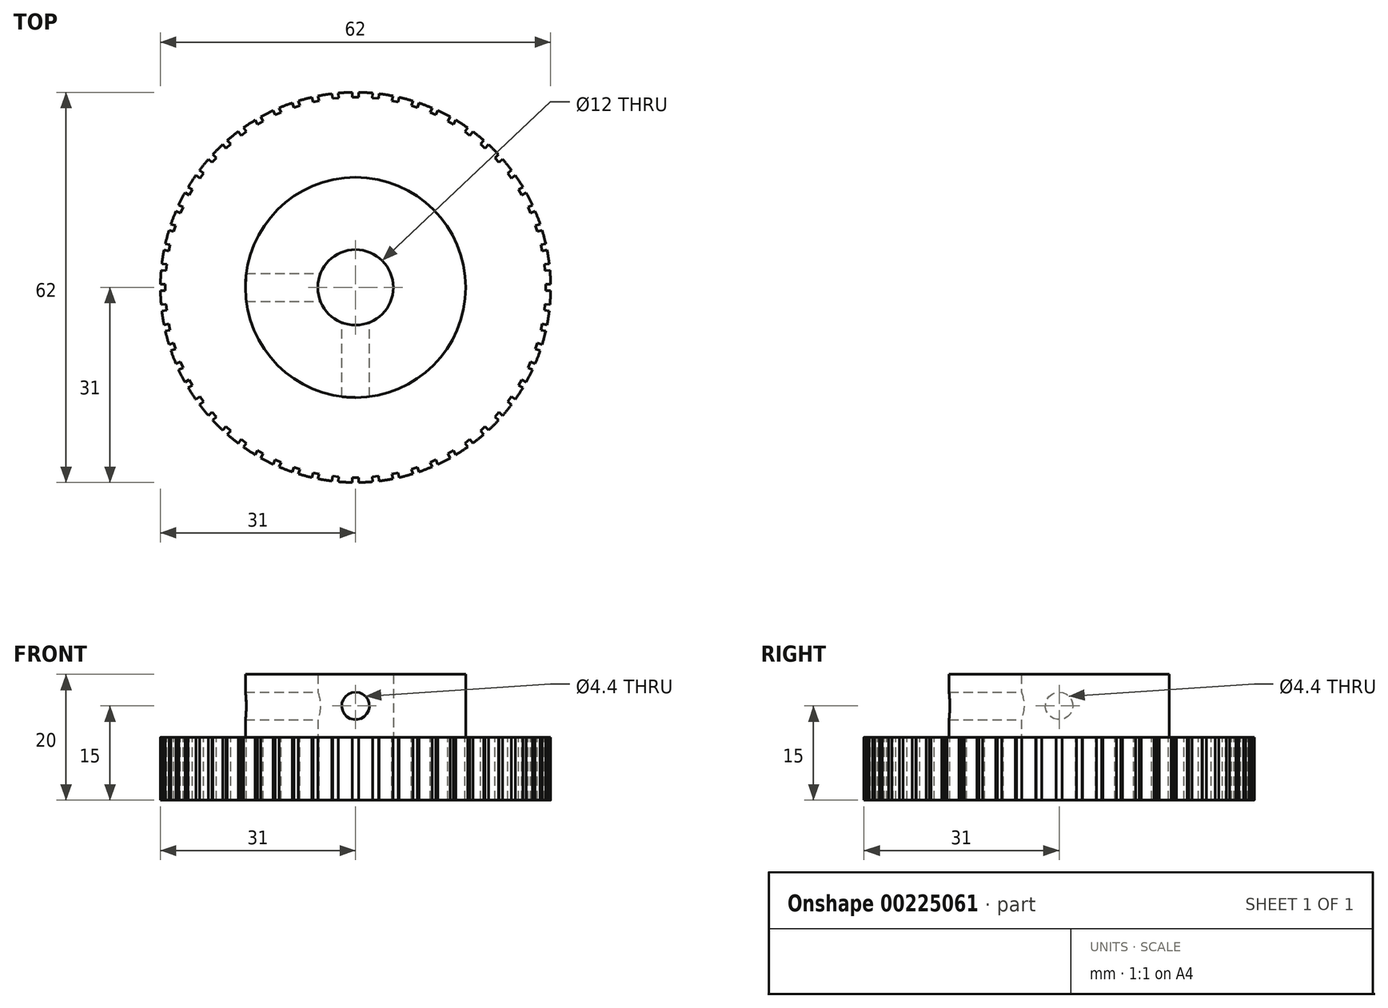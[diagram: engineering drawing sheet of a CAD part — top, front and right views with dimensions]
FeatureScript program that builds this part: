
annotation { "Feature Type Name" : "Feature", "Feature Type Description" : "" }
export const myFeature = defineFeature(function(context is Context, id is Id, definition is map)
    precondition{}
    {
        {
            var Q0;
            Q0=qCreatedBy(makeId("Top.planeOp"),FACE);
            var sketch = newSketch(context, id + "F0", { "sketchPlane" : qUnion([Q0])});
            skCircle(sketch, "E0", {"center": v(0, 0) * mm, "radius": 31 * mm});
            skCircle(sketch, "E1", {"center": v(0, 0) * mm, "radius": 6 * mm});
            skSolve(sketch);
        }
        {
            var Q0;
            Q0=qSketchRegion(id+"F0",true);
            extrude(context, id + "F1", {"entities" : qUnion([Q0]), "depth" : 10 * mm});
        }
        {
            var Q0;
            Q0=makeQuery(id+"F1.opExtrude","CAP_FACE",FACE,{"disambiguationData":[OSD([sQuery(id+"F0.wireOp",EDGE,"E0"),sQuery(id+"F0.wireOp",EDGE,"E1")])],"isStart":false});
            var sketch = newSketch(context, id + "F2", { "sketchPlane" : qUnion([Q0])});
            skCircle(sketch, "E2", {"center": v(0, 0) * mm, "radius": 17.5 * mm});
            skCircle(sketch, "E3", {"center": v(0, 0) * mm, "radius": 6 * mm});
            skSolve(sketch);
        }
        {
            var Q0;
            Q0=qSketchRegion(id+"F2",true);
            extrude(context, id + "F3", {"entities" : qUnion([Q0]), "operationType" : NewBodyOperationType.ADD, "depth" : 10 * mm});
        }
        {
            var Q0;
            Q0=makeQuery(id+"F1.opExtrude","CAP_FACE",FACE,{"disambiguationData":[OSD([sQuery(id+"F0.wireOp",EDGE,"E0"),sQuery(id+"F0.wireOp",EDGE,"E1")])],"isStart":false});
            var sketch = newSketch(context, id + "F4", { "sketchPlane" : qUnion([Q0])});
            skLineSegment(sketch, "E4.bottom", {"start": v(-0.5, 35.22) * mm, "end": v(0.5, 35.22) * mm});
            skLineSegment(sketch, "E4.top", {"start": v(-0.5, 30.22) * mm, "end": v(0.5, 30.22) * mm});
            skLineSegment(sketch, "E4.left", {"start": v(-0.5, 35.22) * mm, "end": v(-0.5, 30.22) * mm});
            skLineSegment(sketch, "E4.right", {"start": v(0.5, 35.22) * mm, "end": v(0.5, 30.22) * mm});
            skLineSegment(sketch, "E5.1.0", {"start": v(-3.18, 35.08) * mm, "end": v(-2.66, 30.1) * mm});
            skLineSegment(sketch, "E5.1.1", {"start": v(-4.18, 34.97) * mm, "end": v(-3.66, 30) * mm});
            skLineSegment(sketch, "E5.1.2", {"start": v(-3.66, 30) * mm, "end": v(-2.66, 30.1) * mm});
            skLineSegment(sketch, "E5.1.3", {"start": v(-4.18, 34.97) * mm, "end": v(-3.18, 35.08) * mm});
            skLineSegment(sketch, "E5.2.0", {"start": v(-6.83, 34.55) * mm, "end": v(-5.8, 29.66) * mm});
            skLineSegment(sketch, "E5.2.1", {"start": v(-7.81, 34.34) * mm, "end": v(-6.77, 29.45) * mm});
            skLineSegment(sketch, "E5.2.2", {"start": v(-6.77, 29.45) * mm, "end": v(-5.8, 29.66) * mm});
            skLineSegment(sketch, "E5.2.3", {"start": v(-7.81, 34.34) * mm, "end": v(-6.83, 34.55) * mm});
            skLineSegment(sketch, "E5.3.0", {"start": v(-10.4, 33.65) * mm, "end": v(-8.86, 28.9) * mm});
            skLineSegment(sketch, "E5.3.1", {"start": v(-11.36, 33.34) * mm, "end": v(-9.81, 28.58) * mm});
            skLineSegment(sketch, "E5.3.2", {"start": v(-9.81, 28.58) * mm, "end": v(-8.86, 28.9) * mm});
            skLineSegment(sketch, "E5.3.3", {"start": v(-11.36, 33.34) * mm, "end": v(-10.4, 33.65) * mm});
            skLineSegment(sketch, "E5.4.0", {"start": v(-13.87, 32.38) * mm, "end": v(-11.83, 27.8) * mm});
            skLineSegment(sketch, "E5.4.1", {"start": v(-14.78, 31.97) * mm, "end": v(-12.75, 27.4) * mm});
            skLineSegment(sketch, "E5.4.2", {"start": v(-12.75, 27.4) * mm, "end": v(-11.83, 27.8) * mm});
            skLineSegment(sketch, "E5.4.3", {"start": v(-14.78, 31.97) * mm, "end": v(-13.87, 32.38) * mm});
            skLineSegment(sketch, "E5.5.0", {"start": v(-17.18, 30.75) * mm, "end": v(-14.68, 26.42) * mm});
            skLineSegment(sketch, "E5.5.1", {"start": v(-18.04, 30.25) * mm, "end": v(-15.54, 25.92) * mm});
            skLineSegment(sketch, "E5.5.2", {"start": v(-15.54, 25.92) * mm, "end": v(-14.68, 26.42) * mm});
            skLineSegment(sketch, "E5.5.3", {"start": v(-18.04, 30.25) * mm, "end": v(-17.18, 30.75) * mm});
            skLineSegment(sketch, "E5.6.0", {"start": v(-20.3, 28.78) * mm, "end": v(-17.36, 24.74) * mm});
            skLineSegment(sketch, "E5.6.1", {"start": v(-21.1, 28.2) * mm, "end": v(-18.17, 24.15) * mm});
            skLineSegment(sketch, "E5.6.2", {"start": v(-18.17, 24.15) * mm, "end": v(-17.36, 24.74) * mm});
            skLineSegment(sketch, "E5.6.3", {"start": v(-21.1, 28.2) * mm, "end": v(-20.3, 28.78) * mm});
            skLineSegment(sketch, "E5.7.0", {"start": v(-23.2, 26.5) * mm, "end": v(-19.85, 22.8) * mm});
            skLineSegment(sketch, "E5.7.1", {"start": v(-23.94, 25.84) * mm, "end": v(-20.6, 22.12) * mm});
            skLineSegment(sketch, "E5.7.2", {"start": v(-20.6, 22.12) * mm, "end": v(-19.85, 22.8) * mm});
            skLineSegment(sketch, "E5.7.3", {"start": v(-23.94, 25.84) * mm, "end": v(-23.2, 26.5) * mm});
            skLineSegment(sketch, "E5.8.0", {"start": v(-25.84, 23.94) * mm, "end": v(-22.12, 20.6) * mm});
            skLineSegment(sketch, "E5.8.1", {"start": v(-26.5, 23.2) * mm, "end": v(-22.8, 19.85) * mm});
            skLineSegment(sketch, "E5.8.2", {"start": v(-22.8, 19.85) * mm, "end": v(-22.12, 20.6) * mm});
            skLineSegment(sketch, "E5.8.3", {"start": v(-26.5, 23.2) * mm, "end": v(-25.84, 23.94) * mm});
            skLineSegment(sketch, "E5.9.0", {"start": v(-28.2, 21.1) * mm, "end": v(-24.15, 18.17) * mm});
            skLineSegment(sketch, "E5.9.1", {"start": v(-28.78, 20.3) * mm, "end": v(-24.74, 17.36) * mm});
            skLineSegment(sketch, "E5.9.2", {"start": v(-24.74, 17.36) * mm, "end": v(-24.15, 18.17) * mm});
            skLineSegment(sketch, "E5.9.3", {"start": v(-28.78, 20.3) * mm, "end": v(-28.2, 21.1) * mm});
            skLineSegment(sketch, "E5.10.0", {"start": v(-30.25, 18.04) * mm, "end": v(-25.92, 15.54) * mm});
            skLineSegment(sketch, "E5.10.1", {"start": v(-30.75, 17.18) * mm, "end": v(-26.42, 14.68) * mm});
            skLineSegment(sketch, "E5.10.2", {"start": v(-26.42, 14.68) * mm, "end": v(-25.92, 15.54) * mm});
            skLineSegment(sketch, "E5.10.3", {"start": v(-30.75, 17.18) * mm, "end": v(-30.25, 18.04) * mm});
            skLineSegment(sketch, "E5.11.0", {"start": v(-31.97, 14.78) * mm, "end": v(-27.4, 12.75) * mm});
            skLineSegment(sketch, "E5.11.1", {"start": v(-32.38, 13.87) * mm, "end": v(-27.8, 11.83) * mm});
            skLineSegment(sketch, "E5.11.2", {"start": v(-27.8, 11.83) * mm, "end": v(-27.4, 12.75) * mm});
            skLineSegment(sketch, "E5.11.3", {"start": v(-32.38, 13.87) * mm, "end": v(-31.97, 14.78) * mm});
            skLineSegment(sketch, "E5.12.0", {"start": v(-33.34, 11.36) * mm, "end": v(-28.58, 9.81) * mm});
            skLineSegment(sketch, "E5.12.1", {"start": v(-33.65, 10.4) * mm, "end": v(-28.9, 8.86) * mm});
            skLineSegment(sketch, "E5.12.2", {"start": v(-28.9, 8.86) * mm, "end": v(-28.58, 9.81) * mm});
            skLineSegment(sketch, "E5.12.3", {"start": v(-33.65, 10.4) * mm, "end": v(-33.34, 11.36) * mm});
            skLineSegment(sketch, "E5.13.0", {"start": v(-34.34, 7.81) * mm, "end": v(-29.45, 6.77) * mm});
            skLineSegment(sketch, "E5.13.1", {"start": v(-34.55, 6.83) * mm, "end": v(-29.66, 5.8) * mm});
            skLineSegment(sketch, "E5.13.2", {"start": v(-29.66, 5.8) * mm, "end": v(-29.45, 6.77) * mm});
            skLineSegment(sketch, "E5.13.3", {"start": v(-34.55, 6.83) * mm, "end": v(-34.34, 7.81) * mm});
            skLineSegment(sketch, "E5.14.0", {"start": v(-34.97, 4.18) * mm, "end": v(-30, 3.66) * mm});
            skLineSegment(sketch, "E5.14.1", {"start": v(-35.08, 3.18) * mm, "end": v(-30.1, 2.66) * mm});
            skLineSegment(sketch, "E5.14.2", {"start": v(-30.1, 2.66) * mm, "end": v(-30, 3.66) * mm});
            skLineSegment(sketch, "E5.14.3", {"start": v(-35.08, 3.18) * mm, "end": v(-34.97, 4.18) * mm});
            skLineSegment(sketch, "E5.15.0", {"start": v(-35.22, 0.5) * mm, "end": v(-30.22, 0.5) * mm});
            skLineSegment(sketch, "E5.15.1", {"start": v(-35.22, -0.5) * mm, "end": v(-30.22, -0.5) * mm});
            skLineSegment(sketch, "E5.15.2", {"start": v(-30.22, -0.5) * mm, "end": v(-30.22, 0.5) * mm});
            skLineSegment(sketch, "E5.15.3", {"start": v(-35.22, -0.5) * mm, "end": v(-35.22, 0.5) * mm});
            skLineSegment(sketch, "E5.16.0", {"start": v(-35.08, -3.18) * mm, "end": v(-30.1, -2.66) * mm});
            skLineSegment(sketch, "E5.16.1", {"start": v(-34.97, -4.18) * mm, "end": v(-30, -3.66) * mm});
            skLineSegment(sketch, "E5.16.2", {"start": v(-30, -3.66) * mm, "end": v(-30.1, -2.66) * mm});
            skLineSegment(sketch, "E5.16.3", {"start": v(-34.97, -4.18) * mm, "end": v(-35.08, -3.18) * mm});
            skLineSegment(sketch, "E5.17.0", {"start": v(-34.55, -6.83) * mm, "end": v(-29.66, -5.8) * mm});
            skLineSegment(sketch, "E5.17.1", {"start": v(-34.34, -7.81) * mm, "end": v(-29.45, -6.77) * mm});
            skLineSegment(sketch, "E5.17.2", {"start": v(-29.45, -6.77) * mm, "end": v(-29.66, -5.8) * mm});
            skLineSegment(sketch, "E5.17.3", {"start": v(-34.34, -7.81) * mm, "end": v(-34.55, -6.83) * mm});
            skLineSegment(sketch, "E5.18.0", {"start": v(-33.65, -10.4) * mm, "end": v(-28.9, -8.86) * mm});
            skLineSegment(sketch, "E5.18.1", {"start": v(-33.34, -11.36) * mm, "end": v(-28.58, -9.81) * mm});
            skLineSegment(sketch, "E5.18.2", {"start": v(-28.58, -9.81) * mm, "end": v(-28.9, -8.86) * mm});
            skLineSegment(sketch, "E5.18.3", {"start": v(-33.34, -11.36) * mm, "end": v(-33.65, -10.4) * mm});
            skLineSegment(sketch, "E5.19.0", {"start": v(-32.38, -13.87) * mm, "end": v(-27.8, -11.83) * mm});
            skLineSegment(sketch, "E5.19.1", {"start": v(-31.97, -14.78) * mm, "end": v(-27.4, -12.75) * mm});
            skLineSegment(sketch, "E5.19.2", {"start": v(-27.4, -12.75) * mm, "end": v(-27.8, -11.83) * mm});
            skLineSegment(sketch, "E5.19.3", {"start": v(-31.97, -14.78) * mm, "end": v(-32.38, -13.87) * mm});
            skLineSegment(sketch, "E5.20.0", {"start": v(-30.75, -17.18) * mm, "end": v(-26.42, -14.68) * mm});
            skLineSegment(sketch, "E5.20.1", {"start": v(-30.25, -18.04) * mm, "end": v(-25.92, -15.54) * mm});
            skLineSegment(sketch, "E5.20.2", {"start": v(-25.92, -15.54) * mm, "end": v(-26.42, -14.68) * mm});
            skLineSegment(sketch, "E5.20.3", {"start": v(-30.25, -18.04) * mm, "end": v(-30.75, -17.18) * mm});
            skLineSegment(sketch, "E5.21.0", {"start": v(-28.78, -20.3) * mm, "end": v(-24.74, -17.36) * mm});
            skLineSegment(sketch, "E5.21.1", {"start": v(-28.2, -21.1) * mm, "end": v(-24.15, -18.17) * mm});
            skLineSegment(sketch, "E5.21.2", {"start": v(-24.15, -18.17) * mm, "end": v(-24.74, -17.36) * mm});
            skLineSegment(sketch, "E5.21.3", {"start": v(-28.2, -21.1) * mm, "end": v(-28.78, -20.3) * mm});
            skLineSegment(sketch, "E5.22.0", {"start": v(-26.5, -23.2) * mm, "end": v(-22.8, -19.85) * mm});
            skLineSegment(sketch, "E5.22.1", {"start": v(-25.84, -23.94) * mm, "end": v(-22.12, -20.6) * mm});
            skLineSegment(sketch, "E5.22.2", {"start": v(-22.12, -20.6) * mm, "end": v(-22.8, -19.85) * mm});
            skLineSegment(sketch, "E5.22.3", {"start": v(-25.84, -23.94) * mm, "end": v(-26.5, -23.2) * mm});
            skLineSegment(sketch, "E5.23.0", {"start": v(-23.94, -25.84) * mm, "end": v(-20.6, -22.12) * mm});
            skLineSegment(sketch, "E5.23.1", {"start": v(-23.2, -26.5) * mm, "end": v(-19.85, -22.8) * mm});
            skLineSegment(sketch, "E5.23.2", {"start": v(-19.85, -22.8) * mm, "end": v(-20.6, -22.12) * mm});
            skLineSegment(sketch, "E5.23.3", {"start": v(-23.2, -26.5) * mm, "end": v(-23.94, -25.84) * mm});
            skLineSegment(sketch, "E5.24.0", {"start": v(-21.1, -28.2) * mm, "end": v(-18.17, -24.15) * mm});
            skLineSegment(sketch, "E5.24.1", {"start": v(-20.3, -28.78) * mm, "end": v(-17.36, -24.74) * mm});
            skLineSegment(sketch, "E5.24.2", {"start": v(-17.36, -24.74) * mm, "end": v(-18.17, -24.15) * mm});
            skLineSegment(sketch, "E5.24.3", {"start": v(-20.3, -28.78) * mm, "end": v(-21.1, -28.2) * mm});
            skLineSegment(sketch, "E5.25.0", {"start": v(-18.04, -30.25) * mm, "end": v(-15.54, -25.92) * mm});
            skLineSegment(sketch, "E5.25.1", {"start": v(-17.18, -30.75) * mm, "end": v(-14.68, -26.42) * mm});
            skLineSegment(sketch, "E5.25.2", {"start": v(-14.68, -26.42) * mm, "end": v(-15.54, -25.92) * mm});
            skLineSegment(sketch, "E5.25.3", {"start": v(-17.18, -30.75) * mm, "end": v(-18.04, -30.25) * mm});
            skLineSegment(sketch, "E5.26.0", {"start": v(-14.78, -31.97) * mm, "end": v(-12.75, -27.4) * mm});
            skLineSegment(sketch, "E5.26.1", {"start": v(-13.87, -32.38) * mm, "end": v(-11.83, -27.8) * mm});
            skLineSegment(sketch, "E5.26.2", {"start": v(-11.83, -27.8) * mm, "end": v(-12.75, -27.4) * mm});
            skLineSegment(sketch, "E5.26.3", {"start": v(-13.87, -32.38) * mm, "end": v(-14.78, -31.97) * mm});
            skLineSegment(sketch, "E5.27.0", {"start": v(-11.36, -33.34) * mm, "end": v(-9.81, -28.58) * mm});
            skLineSegment(sketch, "E5.27.1", {"start": v(-10.4, -33.65) * mm, "end": v(-8.86, -28.9) * mm});
            skLineSegment(sketch, "E5.27.2", {"start": v(-8.86, -28.9) * mm, "end": v(-9.81, -28.58) * mm});
            skLineSegment(sketch, "E5.27.3", {"start": v(-10.4, -33.65) * mm, "end": v(-11.36, -33.34) * mm});
            skLineSegment(sketch, "E5.28.0", {"start": v(-7.81, -34.34) * mm, "end": v(-6.77, -29.45) * mm});
            skLineSegment(sketch, "E5.28.1", {"start": v(-6.83, -34.55) * mm, "end": v(-5.8, -29.66) * mm});
            skLineSegment(sketch, "E5.28.2", {"start": v(-5.8, -29.66) * mm, "end": v(-6.77, -29.45) * mm});
            skLineSegment(sketch, "E5.28.3", {"start": v(-6.83, -34.55) * mm, "end": v(-7.81, -34.34) * mm});
            skLineSegment(sketch, "E5.29.0", {"start": v(-4.18, -34.97) * mm, "end": v(-3.66, -30) * mm});
            skLineSegment(sketch, "E5.29.1", {"start": v(-3.18, -35.08) * mm, "end": v(-2.66, -30.1) * mm});
            skLineSegment(sketch, "E5.29.2", {"start": v(-2.66, -30.1) * mm, "end": v(-3.66, -30) * mm});
            skLineSegment(sketch, "E5.29.3", {"start": v(-3.18, -35.08) * mm, "end": v(-4.18, -34.97) * mm});
            skLineSegment(sketch, "E5.30.0", {"start": v(-0.5, -35.22) * mm, "end": v(-0.5, -30.22) * mm});
            skLineSegment(sketch, "E5.30.1", {"start": v(0.5, -35.22) * mm, "end": v(0.5, -30.22) * mm});
            skLineSegment(sketch, "E5.30.2", {"start": v(0.5, -30.22) * mm, "end": v(-0.5, -30.22) * mm});
            skLineSegment(sketch, "E5.30.3", {"start": v(0.5, -35.22) * mm, "end": v(-0.5, -35.22) * mm});
            skLineSegment(sketch, "E5.31.0", {"start": v(3.18, -35.08) * mm, "end": v(2.66, -30.1) * mm});
            skLineSegment(sketch, "E5.31.1", {"start": v(4.18, -34.97) * mm, "end": v(3.66, -30) * mm});
            skLineSegment(sketch, "E5.31.2", {"start": v(3.66, -30) * mm, "end": v(2.66, -30.1) * mm});
            skLineSegment(sketch, "E5.31.3", {"start": v(4.18, -34.97) * mm, "end": v(3.18, -35.08) * mm});
            skLineSegment(sketch, "E5.32.0", {"start": v(6.83, -34.55) * mm, "end": v(5.8, -29.66) * mm});
            skLineSegment(sketch, "E5.32.1", {"start": v(7.81, -34.34) * mm, "end": v(6.77, -29.45) * mm});
            skLineSegment(sketch, "E5.32.2", {"start": v(6.77, -29.45) * mm, "end": v(5.8, -29.66) * mm});
            skLineSegment(sketch, "E5.32.3", {"start": v(7.81, -34.34) * mm, "end": v(6.83, -34.55) * mm});
            skLineSegment(sketch, "E5.33.0", {"start": v(10.4, -33.65) * mm, "end": v(8.86, -28.9) * mm});
            skLineSegment(sketch, "E5.33.1", {"start": v(11.36, -33.34) * mm, "end": v(9.81, -28.58) * mm});
            skLineSegment(sketch, "E5.33.2", {"start": v(9.81, -28.58) * mm, "end": v(8.86, -28.9) * mm});
            skLineSegment(sketch, "E5.33.3", {"start": v(11.36, -33.34) * mm, "end": v(10.4, -33.65) * mm});
            skLineSegment(sketch, "E5.34.0", {"start": v(13.87, -32.38) * mm, "end": v(11.83, -27.8) * mm});
            skLineSegment(sketch, "E5.34.1", {"start": v(14.78, -31.97) * mm, "end": v(12.75, -27.4) * mm});
            skLineSegment(sketch, "E5.34.2", {"start": v(12.75, -27.4) * mm, "end": v(11.83, -27.8) * mm});
            skLineSegment(sketch, "E5.34.3", {"start": v(14.78, -31.97) * mm, "end": v(13.87, -32.38) * mm});
            skLineSegment(sketch, "E5.35.0", {"start": v(17.18, -30.75) * mm, "end": v(14.68, -26.42) * mm});
            skLineSegment(sketch, "E5.35.1", {"start": v(18.04, -30.25) * mm, "end": v(15.54, -25.92) * mm});
            skLineSegment(sketch, "E5.35.2", {"start": v(15.54, -25.92) * mm, "end": v(14.68, -26.42) * mm});
            skLineSegment(sketch, "E5.35.3", {"start": v(18.04, -30.25) * mm, "end": v(17.18, -30.75) * mm});
            skLineSegment(sketch, "E5.36.0", {"start": v(20.3, -28.78) * mm, "end": v(17.36, -24.74) * mm});
            skLineSegment(sketch, "E5.36.1", {"start": v(21.1, -28.2) * mm, "end": v(18.17, -24.15) * mm});
            skLineSegment(sketch, "E5.36.2", {"start": v(18.17, -24.15) * mm, "end": v(17.36, -24.74) * mm});
            skLineSegment(sketch, "E5.36.3", {"start": v(21.1, -28.2) * mm, "end": v(20.3, -28.78) * mm});
            skLineSegment(sketch, "E5.37.0", {"start": v(23.2, -26.5) * mm, "end": v(19.85, -22.8) * mm});
            skLineSegment(sketch, "E5.37.1", {"start": v(23.94, -25.84) * mm, "end": v(20.6, -22.12) * mm});
            skLineSegment(sketch, "E5.37.2", {"start": v(20.6, -22.12) * mm, "end": v(19.85, -22.8) * mm});
            skLineSegment(sketch, "E5.37.3", {"start": v(23.94, -25.84) * mm, "end": v(23.2, -26.5) * mm});
            skLineSegment(sketch, "E5.38.0", {"start": v(25.84, -23.94) * mm, "end": v(22.12, -20.6) * mm});
            skLineSegment(sketch, "E5.38.1", {"start": v(26.5, -23.2) * mm, "end": v(22.8, -19.85) * mm});
            skLineSegment(sketch, "E5.38.2", {"start": v(22.8, -19.85) * mm, "end": v(22.12, -20.6) * mm});
            skLineSegment(sketch, "E5.38.3", {"start": v(26.5, -23.2) * mm, "end": v(25.84, -23.94) * mm});
            skLineSegment(sketch, "E5.39.0", {"start": v(28.2, -21.1) * mm, "end": v(24.15, -18.17) * mm});
            skLineSegment(sketch, "E5.39.1", {"start": v(28.78, -20.3) * mm, "end": v(24.74, -17.36) * mm});
            skLineSegment(sketch, "E5.39.2", {"start": v(24.74, -17.36) * mm, "end": v(24.15, -18.17) * mm});
            skLineSegment(sketch, "E5.39.3", {"start": v(28.78, -20.3) * mm, "end": v(28.2, -21.1) * mm});
            skLineSegment(sketch, "E5.40.0", {"start": v(30.25, -18.04) * mm, "end": v(25.92, -15.54) * mm});
            skLineSegment(sketch, "E5.40.1", {"start": v(30.75, -17.18) * mm, "end": v(26.42, -14.68) * mm});
            skLineSegment(sketch, "E5.40.2", {"start": v(26.42, -14.68) * mm, "end": v(25.92, -15.54) * mm});
            skLineSegment(sketch, "E5.40.3", {"start": v(30.75, -17.18) * mm, "end": v(30.25, -18.04) * mm});
            skLineSegment(sketch, "E5.41.0", {"start": v(31.97, -14.78) * mm, "end": v(27.4, -12.75) * mm});
            skLineSegment(sketch, "E5.41.1", {"start": v(32.38, -13.87) * mm, "end": v(27.8, -11.83) * mm});
            skLineSegment(sketch, "E5.41.2", {"start": v(27.8, -11.83) * mm, "end": v(27.4, -12.75) * mm});
            skLineSegment(sketch, "E5.41.3", {"start": v(32.38, -13.87) * mm, "end": v(31.97, -14.78) * mm});
            skLineSegment(sketch, "E5.42.0", {"start": v(33.34, -11.36) * mm, "end": v(28.58, -9.81) * mm});
            skLineSegment(sketch, "E5.42.1", {"start": v(33.65, -10.4) * mm, "end": v(28.9, -8.86) * mm});
            skLineSegment(sketch, "E5.42.2", {"start": v(28.9, -8.86) * mm, "end": v(28.58, -9.81) * mm});
            skLineSegment(sketch, "E5.42.3", {"start": v(33.65, -10.4) * mm, "end": v(33.34, -11.36) * mm});
            skLineSegment(sketch, "E5.43.0", {"start": v(34.34, -7.81) * mm, "end": v(29.45, -6.77) * mm});
            skLineSegment(sketch, "E5.43.1", {"start": v(34.55, -6.83) * mm, "end": v(29.66, -5.8) * mm});
            skLineSegment(sketch, "E5.43.2", {"start": v(29.66, -5.8) * mm, "end": v(29.45, -6.77) * mm});
            skLineSegment(sketch, "E5.43.3", {"start": v(34.55, -6.83) * mm, "end": v(34.34, -7.81) * mm});
            skLineSegment(sketch, "E5.44.0", {"start": v(34.97, -4.18) * mm, "end": v(30, -3.66) * mm});
            skLineSegment(sketch, "E5.44.1", {"start": v(35.08, -3.18) * mm, "end": v(30.1, -2.66) * mm});
            skLineSegment(sketch, "E5.44.2", {"start": v(30.1, -2.66) * mm, "end": v(30, -3.66) * mm});
            skLineSegment(sketch, "E5.44.3", {"start": v(35.08, -3.18) * mm, "end": v(34.97, -4.18) * mm});
            skLineSegment(sketch, "E5.45.0", {"start": v(35.22, -0.5) * mm, "end": v(30.22, -0.5) * mm});
            skLineSegment(sketch, "E5.45.1", {"start": v(35.22, 0.5) * mm, "end": v(30.22, 0.5) * mm});
            skLineSegment(sketch, "E5.45.2", {"start": v(30.22, 0.5) * mm, "end": v(30.22, -0.5) * mm});
            skLineSegment(sketch, "E5.45.3", {"start": v(35.22, 0.5) * mm, "end": v(35.22, -0.5) * mm});
            skLineSegment(sketch, "E5.46.0", {"start": v(35.08, 3.18) * mm, "end": v(30.1, 2.66) * mm});
            skLineSegment(sketch, "E5.46.1", {"start": v(34.97, 4.18) * mm, "end": v(30, 3.66) * mm});
            skLineSegment(sketch, "E5.46.2", {"start": v(30, 3.66) * mm, "end": v(30.1, 2.66) * mm});
            skLineSegment(sketch, "E5.46.3", {"start": v(34.97, 4.18) * mm, "end": v(35.08, 3.18) * mm});
            skLineSegment(sketch, "E5.47.0", {"start": v(34.55, 6.83) * mm, "end": v(29.66, 5.8) * mm});
            skLineSegment(sketch, "E5.47.1", {"start": v(34.34, 7.81) * mm, "end": v(29.45, 6.77) * mm});
            skLineSegment(sketch, "E5.47.2", {"start": v(29.45, 6.77) * mm, "end": v(29.66, 5.8) * mm});
            skLineSegment(sketch, "E5.47.3", {"start": v(34.34, 7.81) * mm, "end": v(34.55, 6.83) * mm});
            skLineSegment(sketch, "E5.48.0", {"start": v(33.65, 10.4) * mm, "end": v(28.9, 8.86) * mm});
            skLineSegment(sketch, "E5.48.1", {"start": v(33.34, 11.36) * mm, "end": v(28.58, 9.81) * mm});
            skLineSegment(sketch, "E5.48.2", {"start": v(28.58, 9.81) * mm, "end": v(28.9, 8.86) * mm});
            skLineSegment(sketch, "E5.48.3", {"start": v(33.34, 11.36) * mm, "end": v(33.65, 10.4) * mm});
            skLineSegment(sketch, "E5.49.0", {"start": v(32.38, 13.87) * mm, "end": v(27.8, 11.83) * mm});
            skLineSegment(sketch, "E5.49.1", {"start": v(31.97, 14.78) * mm, "end": v(27.4, 12.75) * mm});
            skLineSegment(sketch, "E5.49.2", {"start": v(27.4, 12.75) * mm, "end": v(27.8, 11.83) * mm});
            skLineSegment(sketch, "E5.49.3", {"start": v(31.97, 14.78) * mm, "end": v(32.38, 13.87) * mm});
            skLineSegment(sketch, "E5.50.0", {"start": v(30.75, 17.18) * mm, "end": v(26.42, 14.68) * mm});
            skLineSegment(sketch, "E5.50.1", {"start": v(30.25, 18.04) * mm, "end": v(25.92, 15.54) * mm});
            skLineSegment(sketch, "E5.50.2", {"start": v(25.92, 15.54) * mm, "end": v(26.42, 14.68) * mm});
            skLineSegment(sketch, "E5.50.3", {"start": v(30.25, 18.04) * mm, "end": v(30.75, 17.18) * mm});
            skLineSegment(sketch, "E5.51.0", {"start": v(28.78, 20.3) * mm, "end": v(24.74, 17.36) * mm});
            skLineSegment(sketch, "E5.51.1", {"start": v(28.2, 21.1) * mm, "end": v(24.15, 18.17) * mm});
            skLineSegment(sketch, "E5.51.2", {"start": v(24.15, 18.17) * mm, "end": v(24.74, 17.36) * mm});
            skLineSegment(sketch, "E5.51.3", {"start": v(28.2, 21.1) * mm, "end": v(28.78, 20.3) * mm});
            skLineSegment(sketch, "E5.52.0", {"start": v(26.5, 23.2) * mm, "end": v(22.8, 19.85) * mm});
            skLineSegment(sketch, "E5.52.1", {"start": v(25.84, 23.94) * mm, "end": v(22.12, 20.6) * mm});
            skLineSegment(sketch, "E5.52.2", {"start": v(22.12, 20.6) * mm, "end": v(22.8, 19.85) * mm});
            skLineSegment(sketch, "E5.52.3", {"start": v(25.84, 23.94) * mm, "end": v(26.5, 23.2) * mm});
            skLineSegment(sketch, "E5.53.0", {"start": v(23.94, 25.84) * mm, "end": v(20.6, 22.12) * mm});
            skLineSegment(sketch, "E5.53.1", {"start": v(23.2, 26.5) * mm, "end": v(19.85, 22.8) * mm});
            skLineSegment(sketch, "E5.53.2", {"start": v(19.85, 22.8) * mm, "end": v(20.6, 22.12) * mm});
            skLineSegment(sketch, "E5.53.3", {"start": v(23.2, 26.5) * mm, "end": v(23.94, 25.84) * mm});
            skLineSegment(sketch, "E5.54.0", {"start": v(21.1, 28.2) * mm, "end": v(18.17, 24.15) * mm});
            skLineSegment(sketch, "E5.54.1", {"start": v(20.3, 28.78) * mm, "end": v(17.36, 24.74) * mm});
            skLineSegment(sketch, "E5.54.2", {"start": v(17.36, 24.74) * mm, "end": v(18.17, 24.15) * mm});
            skLineSegment(sketch, "E5.54.3", {"start": v(20.3, 28.78) * mm, "end": v(21.1, 28.2) * mm});
            skLineSegment(sketch, "E5.55.0", {"start": v(18.04, 30.25) * mm, "end": v(15.54, 25.92) * mm});
            skLineSegment(sketch, "E5.55.1", {"start": v(17.18, 30.75) * mm, "end": v(14.68, 26.42) * mm});
            skLineSegment(sketch, "E5.55.2", {"start": v(14.68, 26.42) * mm, "end": v(15.54, 25.92) * mm});
            skLineSegment(sketch, "E5.55.3", {"start": v(17.18, 30.75) * mm, "end": v(18.04, 30.25) * mm});
            skLineSegment(sketch, "E5.56.0", {"start": v(14.78, 31.97) * mm, "end": v(12.75, 27.4) * mm});
            skLineSegment(sketch, "E5.56.1", {"start": v(13.87, 32.38) * mm, "end": v(11.83, 27.8) * mm});
            skLineSegment(sketch, "E5.56.2", {"start": v(11.83, 27.8) * mm, "end": v(12.75, 27.4) * mm});
            skLineSegment(sketch, "E5.56.3", {"start": v(13.87, 32.38) * mm, "end": v(14.78, 31.97) * mm});
            skLineSegment(sketch, "E5.57.0", {"start": v(11.36, 33.34) * mm, "end": v(9.81, 28.58) * mm});
            skLineSegment(sketch, "E5.57.1", {"start": v(10.4, 33.65) * mm, "end": v(8.86, 28.9) * mm});
            skLineSegment(sketch, "E5.57.2", {"start": v(8.86, 28.9) * mm, "end": v(9.81, 28.58) * mm});
            skLineSegment(sketch, "E5.57.3", {"start": v(10.4, 33.65) * mm, "end": v(11.36, 33.34) * mm});
            skLineSegment(sketch, "E5.58.0", {"start": v(7.81, 34.34) * mm, "end": v(6.77, 29.45) * mm});
            skLineSegment(sketch, "E5.58.1", {"start": v(6.83, 34.55) * mm, "end": v(5.8, 29.66) * mm});
            skLineSegment(sketch, "E5.58.2", {"start": v(5.8, 29.66) * mm, "end": v(6.77, 29.45) * mm});
            skLineSegment(sketch, "E5.58.3", {"start": v(6.83, 34.55) * mm, "end": v(7.81, 34.34) * mm});
            skLineSegment(sketch, "E5.59.0", {"start": v(4.18, 34.97) * mm, "end": v(3.66, 30) * mm});
            skLineSegment(sketch, "E5.59.1", {"start": v(3.18, 35.08) * mm, "end": v(2.66, 30.1) * mm});
            skLineSegment(sketch, "E5.59.2", {"start": v(2.66, 30.1) * mm, "end": v(3.66, 30) * mm});
            skLineSegment(sketch, "E5.59.3", {"start": v(3.18, 35.08) * mm, "end": v(4.18, 34.97) * mm});
            skPoint(sketch, "E5.center", {"position": v(0, 0) * mm});
            skSolve(sketch);
        }
        {
            var Q0;
            Q0=qSketchRegion(id+"F4",true);
            extrude(context, id + "F5", {"entities" : qUnion([Q0]), "operationType" : NewBodyOperationType.REMOVE, "oppositeDirection" : true, "depth" : 25 * mm});
        }
        {
            var Q0;
            Q0=qCreatedBy(makeId("Front.planeOp"),FACE);
            var sketch = newSketch(context, id + "F6", { "sketchPlane" : qUnion([Q0])});
            skPoint(sketch, "E6", {"position": v(0, 15) * mm});
            skSolve(sketch);
        }
        {
            var Q0;
            Q0=sQuery(id+"F6.wireOp",VERTEX,"E6");
            var Q1;
            Q1=makeQuery(id+"F1.opExtrude","SWEPT_BODY",BODY,{"disambiguationData":[OSD([sQuery(id+"F0.wireOp",EDGE,"E0"),sQuery(id+"F0.wireOp",EDGE,"E1")])]});
            hole(context, id + "F7", {"style" : HoleStyle.SIMPLE, "endStyle" : HoleEndStyle.THROUGH, "oppositeDirection" : true, "standardTappedOrClearance" : lookupTablePath({ "standard" : "ISO", "fit" : "Normal", "size" : "M4", "type" : "Clearance" }), "standardBlindInLast" : lookupTablePath({ "fit" : "Standard", "standard" : "ISO", "size" : "M4", "type" : "Clearance" }), "holeDiameter" : 4.4 * mm, "locations" : qUnion([Q0]), "scope" : qUnion([Q1]), "isTappedThrough" : true});
        }
        {
            var Q0;
            Q0=qCreatedBy(makeId("Right.planeOp"),FACE);
            var sketch = newSketch(context, id + "F8", { "sketchPlane" : qUnion([Q0])});
            skPoint(sketch, "E7", {"position": v(0, 15) * mm});
            skSolve(sketch);
        }
        {
            var Q0;
            Q0=sQuery(id+"F8.wireOp",VERTEX,"E7");
            var Q1;
            Q1=makeQuery(id+"F1.opExtrude","SWEPT_BODY",BODY,{"disambiguationData":[OSD([sQuery(id+"F0.wireOp",EDGE,"E0"),sQuery(id+"F0.wireOp",EDGE,"E1")])]});
            hole(context, id + "F9", {"style" : HoleStyle.SIMPLE, "endStyle" : HoleEndStyle.THROUGH, "standardTappedOrClearance" : lookupTablePath({ "standard" : "ISO", "fit" : "Normal", "size" : "M4", "type" : "Clearance" }), "standardBlindInLast" : lookupTablePath({ "fit" : "Standard", "standard" : "ISO", "size" : "M4", "type" : "Clearance" }), "holeDiameter" : 4.4 * mm, "locations" : qUnion([Q0]), "scope" : qUnion([Q1]), "isTappedThrough" : true});
        }
    });
